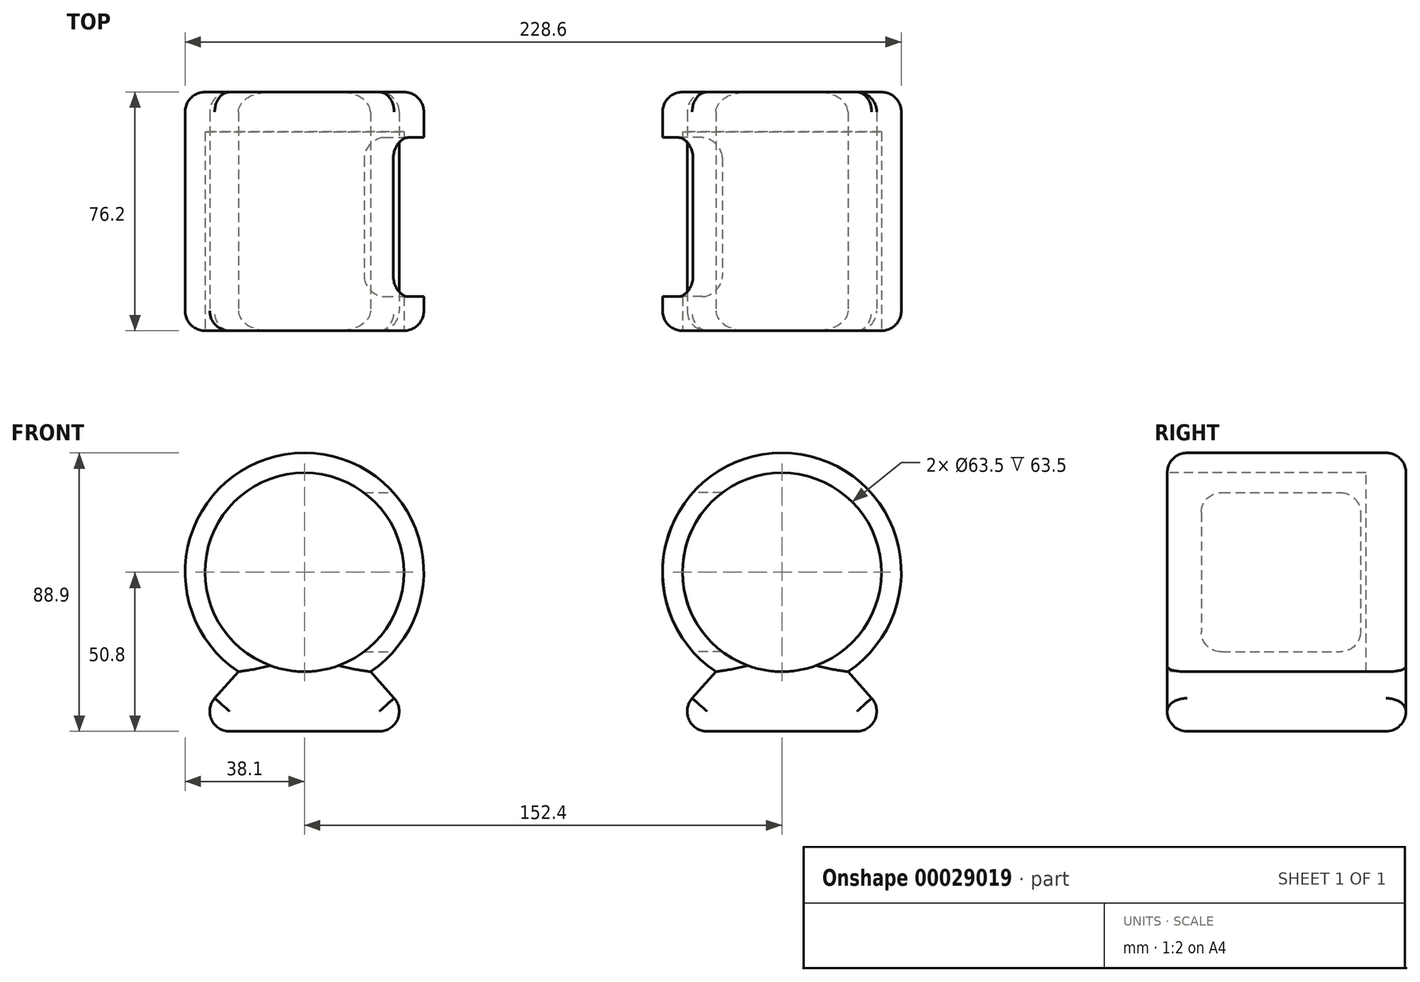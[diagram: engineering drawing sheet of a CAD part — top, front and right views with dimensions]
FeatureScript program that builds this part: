
annotation { "Feature Type Name" : "Feature", "Feature Type Description" : "" }
export const myFeature = defineFeature(function(context is Context, id is Id, definition is map)
    precondition{}
    {
        {
            var Q0;
            Q0=qCreatedBy(makeId("Front.planeOp"),FACE);
            var sketch = newSketch(context, id + "F0", { "sketchPlane" : qUnion([Q0])});
            skCircle(sketch, "E0", {"center": v(0, 0) * mm, "radius": 38.1 * mm});
            skSolve(sketch);
        }
        {
            var Q0;
            Q0=makeQuery(id+"F0.imprint","IMPRINT",FACE,{"disambiguationData":[TD([[makeQuery(id+"F0.imprint","IMPRINT",EDGE,{"derivedFrom":sQuery(id+"F0.wireOp",EDGE,"E0")}),1.0]])]});
            extrude(context, id + "F1", {"entities" : qUnion([Q0]), "depth" : 76.2 * mm});
        }
        {
            var Q0;
            Q0=makeQuery(id+"F1.opExtrude","CAP_FACE",FACE,{"disambiguationData":[OSD([sQuery(id+"F0.wireOp",EDGE,"E0")])],"isStart":false});
            var sketch = newSketch(context, id + "F2", { "sketchPlane" : qUnion([Q0])});
            skCircle(sketch, "E1", {"center": v(0, 0) * mm, "radius": 31.75 * mm});
            skLineSegment(sketch, "E2", {"start": v(0, 0) * mm, "end": v(53.96, 0) * mm, "construction": true});
            skLineSegment(sketch, "E3", {"start": v(53.96, 0) * mm, "end": v(-71.33, 0) * mm, "construction": true});
            skSolve(sketch);
        }
        {
            var Q0;
            Q0=makeQuery(id+"F1.opExtrude","CAP_FACE",FACE,{"disambiguationData":[OSD([sQuery(id+"F0.wireOp",EDGE,"E0")])],"isStart":false});
            var sketch = newSketch(context, id + "F3", { "sketchPlane" : qUnion([Q0])});
            skLineSegment(sketch, "E4", {"start": v(-21.06, -31.75) * mm, "end": v(21.06, -31.75) * mm});
            skLineSegment(sketch, "E5", {"start": v(-21.06, -31.75) * mm, "end": v(-38.1, -50.8) * mm});
            skLineSegment(sketch, "E6", {"start": v(-38.1, -50.8) * mm, "end": v(38.1, -50.8) * mm});
            skLineSegment(sketch, "E7", {"start": v(38.1, -50.8) * mm, "end": v(21.06, -31.75) * mm});
            skSolve(sketch);
        }
        {
            var Q0;
            {var subQ3=sQuery(id+"F3.wireOp",EDGE,"E5");Q0=makeQuery(id+"F3.imprint","IMPRINT",FACE,{"disambiguationData":[TD([[makeQuery(id+"F3.imprint","IMPRINT",EDGE,{"derivedFrom":subQ3}),1.0]])]});}
            var Q1;
            Q1=makeQuery(id+"F1.opExtrude","CAP_FACE",FACE,{"disambiguationData":[OSD([sQuery(id+"F0.wireOp",EDGE,"E0")])],"isStart":true});
            extrude(context, id + "F4", {"entities" : qUnion([Q0]), "operationType" : NewBodyOperationType.ADD, "endBound" : BoundingType.UP_TO_SURFACE, "oppositeDirection" : true, "endBoundEntityFace" : qUnion([Q1]), "depth" : 25.4 * mm});
        }
        {
            var Q0;
            Q0=makeQuery(id+"F1.opExtrude","CAP_EDGE",EDGE,{"disambiguationData":[OSD([sQuery(id+"F0.wireOp",EDGE,"E0")])],"isStart":false});
            var Q1;
            Q1=makeQuery(id+"F1iN863pALH7xxS_1.boolean.opBoolean","COPY",EDGE,{"derivedFrom":makeQuery(id+"F1iN863pALH7xxS_1.opExtrude","CAP_EDGE",EDGE,{"disambiguationData":[OSD([sQuery(id+"F2.wireOp",EDGE,"E1")])],"isStart":true})});
            var Q2;
            Q2=makeQuery(id+"F4.opExtrude","CAP_EDGE",EDGE,{"disambiguationData":[OSD([sQuery(id+"F3.wireOp",EDGE,"E7")])],"isStart":true});
            var Q3;
            Q3=makeQuery(id+"F4.opExtrude","CAP_EDGE",EDGE,{"disambiguationData":[OSD([sQuery(id+"F3.wireOp",EDGE,"E6")])],"isStart":true});
            var Q4;
            Q4=makeQuery(id+"F4.opExtrude","CAP_EDGE",EDGE,{"disambiguationData":[OSD([sQuery(id+"F3.wireOp",EDGE,"E5")])],"isStart":true});
            fillet(context, id + "F5", {"entities" : qUnion([Q0, Q1, Q2, Q3, Q4]), "radius" : 6.35 * mm, "tangentPropagation" : true, "allowEdgeOverflow" : false});
        }
        {
            var Q0;
            Q0=makeQuery(id+"F1.opExtrude","CAP_EDGE",EDGE,{"disambiguationData":[OSD([sQuery(id+"F0.wireOp",EDGE,"E0")])],"isStart":true});
            var Q1;
            Q1=makeQuery(id+"F4.opExtrude","CAP_EDGE",EDGE,{"disambiguationData":[OSD([sQuery(id+"F3.wireOp",EDGE,"E5")])],"isStart":false});
            var Q2;
            Q2=makeQuery(id+"F4.opExtrude","CAP_EDGE",EDGE,{"disambiguationData":[OSD([sQuery(id+"F3.wireOp",EDGE,"E6")])],"isStart":false});
            var Q3;
            Q3=makeQuery(id+"F4.opExtrude","CAP_EDGE",EDGE,{"disambiguationData":[OSD([sQuery(id+"F3.wireOp",EDGE,"E7")])],"isStart":false});
            fillet(context, id + "F6", {"entities" : qUnion([Q0, Q1, Q2, Q3]), "radius" : 6.35 * mm, "tangentPropagation" : true, "allowEdgeOverflow" : false});
        }
        {
            var Q0;
            Q0=makeQuery(id+"F4.opExtrude","SWEPT_EDGE",EDGE,{"disambiguationData":[OSD([sQuery(id+"F3.wireOp",EDGE,"E5"),sQuery(id+"F3.wireOp",EDGE,"E6")])]});
            var Q1;
            Q1=makeQuery(id+"F4.opExtrude","SWEPT_EDGE",EDGE,{"disambiguationData":[OSD([sQuery(id+"F3.wireOp",EDGE,"E6"),sQuery(id+"F3.wireOp",EDGE,"E7")])]});
            fillet(context, id + "F7", {"entities" : qUnion([Q0, Q1]), "radius" : 6.35 * mm, "tangentPropagation" : true, "allowEdgeOverflow" : false});
        }
        {
            var Q0;
            Q0 = qSketchRegion(id + "F2", true);
            extrude(context, id + "F8", {"entities" : qUnion([Q0]), "operationType" : NewBodyOperationType.REMOVE, "oppositeDirection" : true, "depth" : 63.5 * mm});
        }
        {
            var Q0;
            Q0=qCreatedBy(makeId("Right.planeOp"),FACE);
            cPlane(context, id + "F9", {"entities" : qUnion([Q0]), "cplaneType" : CPlaneType.OFFSET, "offset" : 38.1 * mm, "width" : 152.4 * mm, "height" : 152.4 * mm});
        }
        {
            var Q0;
            Q0=qCreatedBy(id+"F9.planeOp",FACE);
            var sketch = newSketch(context, id + "F10", { "sketchPlane" : qUnion([Q0])});
            skLineSegment(sketch, "E8.0", {"start": v(-69.85, 38.1) * mm, "end": v(-69.85, -31.75) * mm, "construction": true});
            skLineSegment(sketch, "E9.0", {"start": v(-6.35, -31.75) * mm, "end": v(-6.35, 38.1) * mm, "construction": true});
            skLineSegment(sketch, "E10.0", {"start": v(-6.35, -31.75) * mm, "end": v(-69.85, -31.75) * mm, "construction": true});
            skLineSegment(sketch, "E11", {"start": v(-74.83, 38.1) * mm, "end": v(9.17, 38.1) * mm, "construction": true});
            skLineSegment(sketch, "E12.0", {"start": v(-75.35, 30.97) * mm, "end": v(-75.35, -30.97) * mm, "construction": true});
            skLineSegment(sketch, "E13", {"start": v(-75.35, 0) * mm, "end": v(50.84, 0) * mm});
            skLineSegment(sketch, "E14.rect.bottom", {"start": v(-20.88, -25.4) * mm, "end": v(-58.98, -25.4) * mm});
            skLineSegment(sketch, "E14.rect.top", {"start": v(-20.88, 25.4) * mm, "end": v(-58.98, 25.4) * mm});
            skLineSegment(sketch, "E14.rect.left", {"start": v(-14.53, -19.05) * mm, "end": v(-14.53, 19.05) * mm});
            skLineSegment(sketch, "E14.rect.right", {"start": v(-65.33, -19.05) * mm, "end": v(-65.33, 19.05) * mm});
            skPoint(sketch, "E14.rect.middle", {"position": v(-39.93, 0) * mm});
            skPoint(sketch, "E15.visualSharp", {"position": v(-14.53, 25.4) * mm});
            skArc(sketch, "E15.filletArc", {"start": v(-14.53, 19.05) * mm, "mid": v(-16.4, 23.54) * mm, "end": v(-20.88, 25.4) * mm});
            skPoint(sketch, "E16.visualSharp", {"position": v(-14.53, -25.4) * mm});
            skArc(sketch, "E16.filletArc", {"start": v(-20.88, -25.4) * mm, "mid": v(-16.4, -23.54) * mm, "end": v(-14.53, -19.05) * mm});
            skPoint(sketch, "E17.visualSharp", {"position": v(-65.33, 25.4) * mm});
            skArc(sketch, "E17.filletArc", {"start": v(-58.98, 25.4) * mm, "mid": v(-63.47, 23.54) * mm, "end": v(-65.33, 19.05) * mm});
            skPoint(sketch, "E18.visualSharp", {"position": v(-65.33, -25.4) * mm});
            skArc(sketch, "E18.filletArc", {"start": v(-65.33, -19.05) * mm, "mid": v(-63.47, -23.54) * mm, "end": v(-58.98, -25.4) * mm});
            skLineSegment(sketch, "E19.0", {"start": v(-1.83, -29.83) * mm, "end": v(-1.83, 31.76) * mm});
            skPoint(sketch, "E20.0", {"position": v(-76.2, 0) * mm});
            skSolve(sketch);
        }
        {
            var Q0;
            Q0=makeQuery(id+"F10.imprint","IMPRINT",FACE,{"disambiguationData":[TD([[makeQuery(id+"F10.imprint","IMPRINT",EDGE,{"derivedFrom":sQuery(id+"F10.wireOp",EDGE,"E14.rect.top")}),1.0]])]});
            var Q1;
            Q1=makeQuery(id+"F10.imprint","IMPRINT",FACE,{"disambiguationData":[TD([[makeQuery(id+"F10.imprint","IMPRINT",EDGE,{"derivedFrom":sQuery(id+"F10.wireOp",EDGE,"E14.rect.bottom")}),-1.0]])]});
            var Q2;
            Q2=makeQuery(id+"F8.boolean.opBoolean","COPY",FACE,{"derivedFrom":makeQuery(id+"F8.opExtrude","SWEPT_FACE",FACE,{"disambiguationData":[OSD([sQuery(id+"F2.wireOp",EDGE,"E1")])]})});
            extrude(context, id + "F11", {"entities" : qUnion([Q0, Q1]), "operationType" : NewBodyOperationType.REMOVE, "oppositeDirection" : true, "endBoundEntityFace" : qUnion([Q2]), "depth" : 38.1 * mm});
        }
        {
            var Q0;
            Q0=qCreatedBy(makeId("Right.planeOp"),FACE);
            cPlane(context, id + "F12", {"entities" : qUnion([Q0]), "cplaneType" : CPlaneType.OFFSET, "offset" : 76.2 * mm, "width" : 152.4 * mm, "height" : 152.4 * mm});
        }
        {
            var Q0;
            Q0=makeQuery(id+"F1.opExtrude","SWEPT_BODY",BODY,{"disambiguationData":[OSD([sQuery(id+"F0.wireOp",EDGE,"E0")])]});
            var Q1;
            Q1=qCreatedBy(id+"F12.planeOp",FACE);
            mirror(context, id + "F13", {"entities" : qUnion([Q0]), "mirrorPlane" : qUnion([Q1])});
        }
    });
